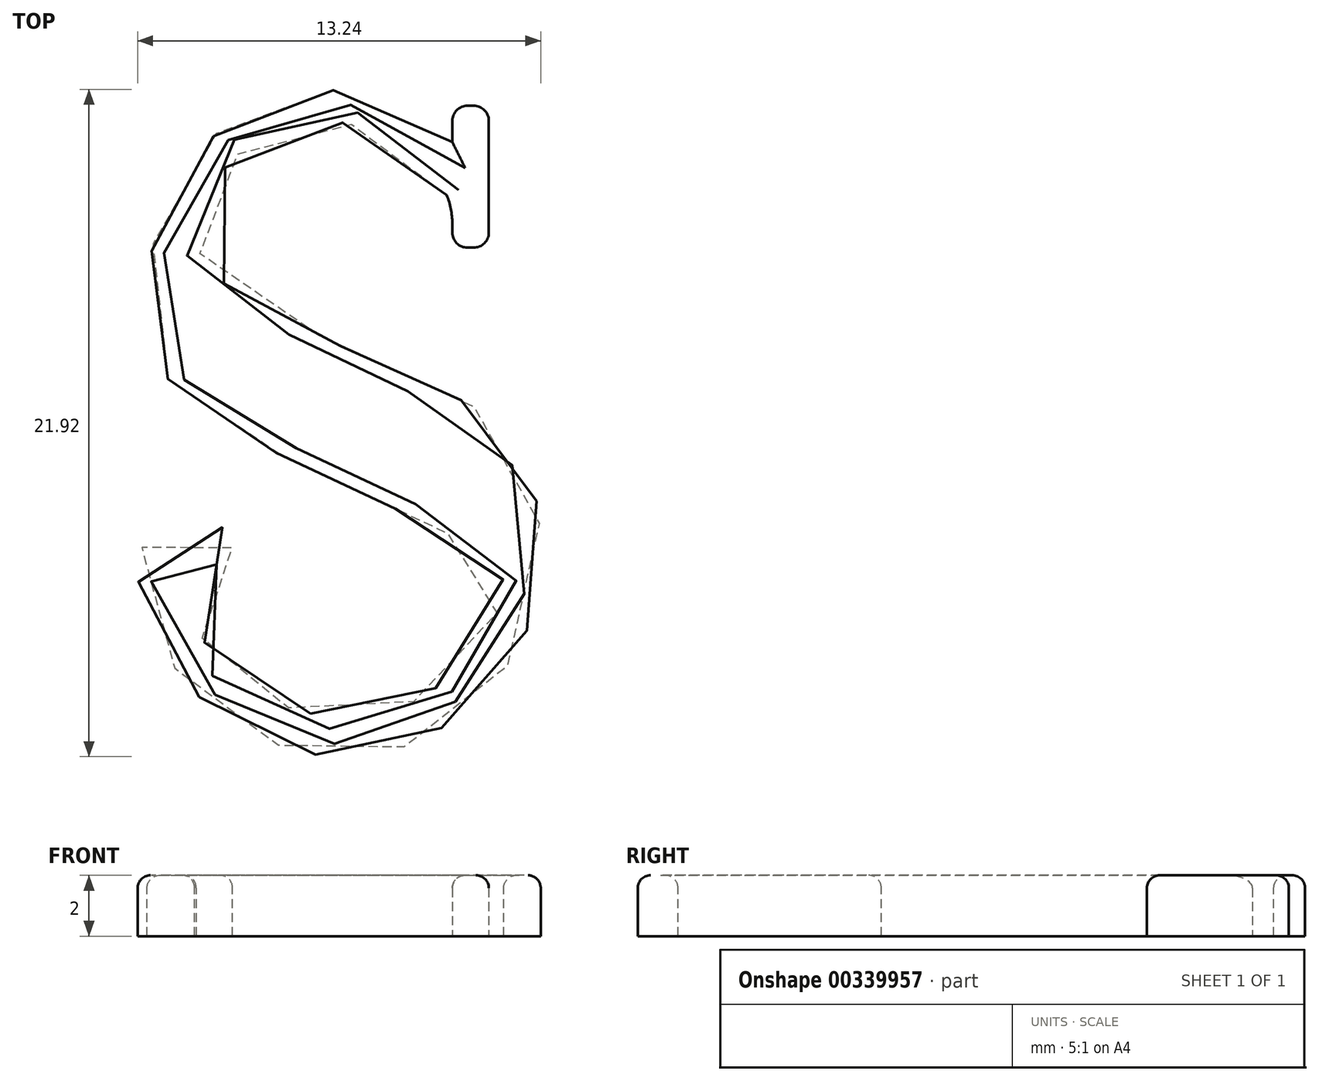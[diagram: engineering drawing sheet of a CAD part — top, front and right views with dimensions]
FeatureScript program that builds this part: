
annotation { "Feature Type Name" : "Feature", "Feature Type Description" : "" }
export const myFeature = defineFeature(function(context is Context, id is Id, definition is map)
    precondition{}
    {
        {
            var Q0;
            Q0=qCreatedBy(makeId("Top.planeOp"),FACE);
            var sketch = newSketch(context, id + "F0", { "sketchPlane" : qUnion([Q0])});
            skLineSegment(sketch, "E0.bottom", {"start": v(3.07, 12.02) * mm, "end": v(4.27, 12.02) * mm});
            skLineSegment(sketch, "E0.top", {"start": v(3.07, 7.35) * mm, "end": v(4.27, 7.35) * mm});
            skLineSegment(sketch, "E0.left", {"start": v(3.07, 12.02) * mm, "end": v(3.07, 7.35) * mm});
            skLineSegment(sketch, "E0.right", {"start": v(4.27, 12.02) * mm, "end": v(4.27, 7.35) * mm});
            skPoint(sketch, "E1.48.internal.snap0", {"position": v(3.07, 9.68) * mm});
            skFitSpline(sketch, "E1", {"points": [v(3.07, 10.82) * mm, v(1.37, 11.94) * mm, v(-0.7, 12.53) * mm, v(-2.68, 12.3) * mm, v(-4.41, 11.34) * mm, v(-5.78, 9.76) * mm, v(-6.61, 8.01) * mm, v(-6.96, 5.97) * mm, v(-6.52, 3.46) * mm, v(-5.29, 2.03) * mm, v(-3.2, 0.85) * mm, v(0.67, -0.99) * mm, v(3.54, -2.35) * mm, v(4.62, -3.21) * mm, v(4.67, -4.3) * mm, v(3.76, -5.85) * mm, v(2.47, -7.17) * mm, v(0.82, -7.9) * mm, v(-1.2, -8.02) * mm, v(-3.04, -7.5) * mm, v(-4.27, -6.68) * mm, v(-5.19, -5.41) * mm, v(-5.32, -4.34) * mm, v(-4.32, -3.3) * mm, v(-4.36, -2) * mm, v(-5.72, -1.38) * mm, v(-7.17, -2.6) * mm, v(-6.9, -4.95) * mm, v(-6.15, -6.34) * mm, v(-4.65, -7.96) * mm, v(-2.9, -8.9) * mm, v(-1.1, -9.34) * mm, v(0.96, -9.2) * mm, v(2.78, -8.38) * mm, v(4.47, -6.88) * mm, v(5.58, -5.08) * mm, v(5.96, -2.2) * mm, v(5.38, 0.46) * mm, v(4.05, 1.96) * mm, v(1.37, 3.2) * mm, v(-2.33, 4.98) * mm, v(-4.64, 6.35) * mm, v(-5.34, 7.66) * mm, v(-4.94, 9.13) * mm, v(-4.05, 10.36) * mm, v(-2.58, 11.3) * mm, v(-0.76, 11.5) * mm, v(1.02, 10.91) * mm, v(2.54, 9.68) * mm, v(3.07, 8.56) * mm], "startDerivative": vector(-78.04, 58.87) * mm, "endDerivative": vector(23.42, -70.14) * mm});
            skSolve(sketch);
        }
        {
            var Q0;
            Q0 = qSketchRegion(id + "F0", true);
            extrude(context, id + "F1", {"entities" : qUnion([Q0]), "depth" : 2 * mm});
        }
        {
            var Q0;
            Q0=makeQuery(id+"F1.opExtrude","SWEPT_EDGE",EDGE,{"disambiguationData":[OSD([sQuery(id+"F0.wireOp",EDGE,"E0.top"),sQuery(id+"F0.wireOp",EDGE,"E0.right")])]});
            var Q1;
            Q1=makeQuery(id+"F1.opExtrude","SWEPT_EDGE",EDGE,{"disambiguationData":[OSD([sQuery(id+"F0.wireOp",EDGE,"E0.top"),sQuery(id+"F0.wireOp",EDGE,"E0.left")])]});
            var Q2;
            Q2=makeQuery(id+"F1.opExtrude","SWEPT_EDGE",EDGE,{"disambiguationData":[OSD([sQuery(id+"F0.wireOp",EDGE,"E0.bottom"),sQuery(id+"F0.wireOp",EDGE,"E0.left")])]});
            var Q3;
            Q3=makeQuery(id+"F1.opExtrude","SWEPT_EDGE",EDGE,{"disambiguationData":[OSD([sQuery(id+"F0.wireOp",EDGE,"E0.bottom"),sQuery(id+"F0.wireOp",EDGE,"E0.right")])]});
            fillet(context, id + "F2", {"entities" : qUnion([Q0, Q1, Q2, Q3]), "radius" : 0.5 * mm, "tangentPropagation" : true, "allowEdgeOverflow" : false});
        }
        {
            var Q0;
            {var subQ0=sQuery(id+"F0.wireOp",EDGE,"E1");var subQ1=sQuery(id+"F0.wireOp",EDGE,"E0.left");Q0=makeQuery(id+"F1.opExtrude","SWEPT_EDGE",EDGE,{"disambiguationData":[OSD([subQ1,subQ0]),TDD([makeQuery(id+"F0.imprint","INTERSECT",VERTEX,{"disambiguationData":[OD(1.0)],"derivedFrom":[subQ1,subQ0]})])]});}
            fillet(context, id + "F3", {"entities" : qUnion([Q0]), "radius" : 2.4 * mm, "tangentPropagation" : true, "allowEdgeOverflow" : false});
        }
        {
            var Q0;
            Q0=makeQuery(id+"F1.opExtrude","CAP_EDGE",EDGE,{"disambiguationData":[OSD([sQuery(id+"F0.wireOp",EDGE,"E1")])],"isStart":false});
            fillet(context, id + "F4", {"entities" : qUnion([Q0]), "radius" : 0.42 * mm, "tangentPropagation" : true, "allowEdgeOverflow" : false});
        }
    });
